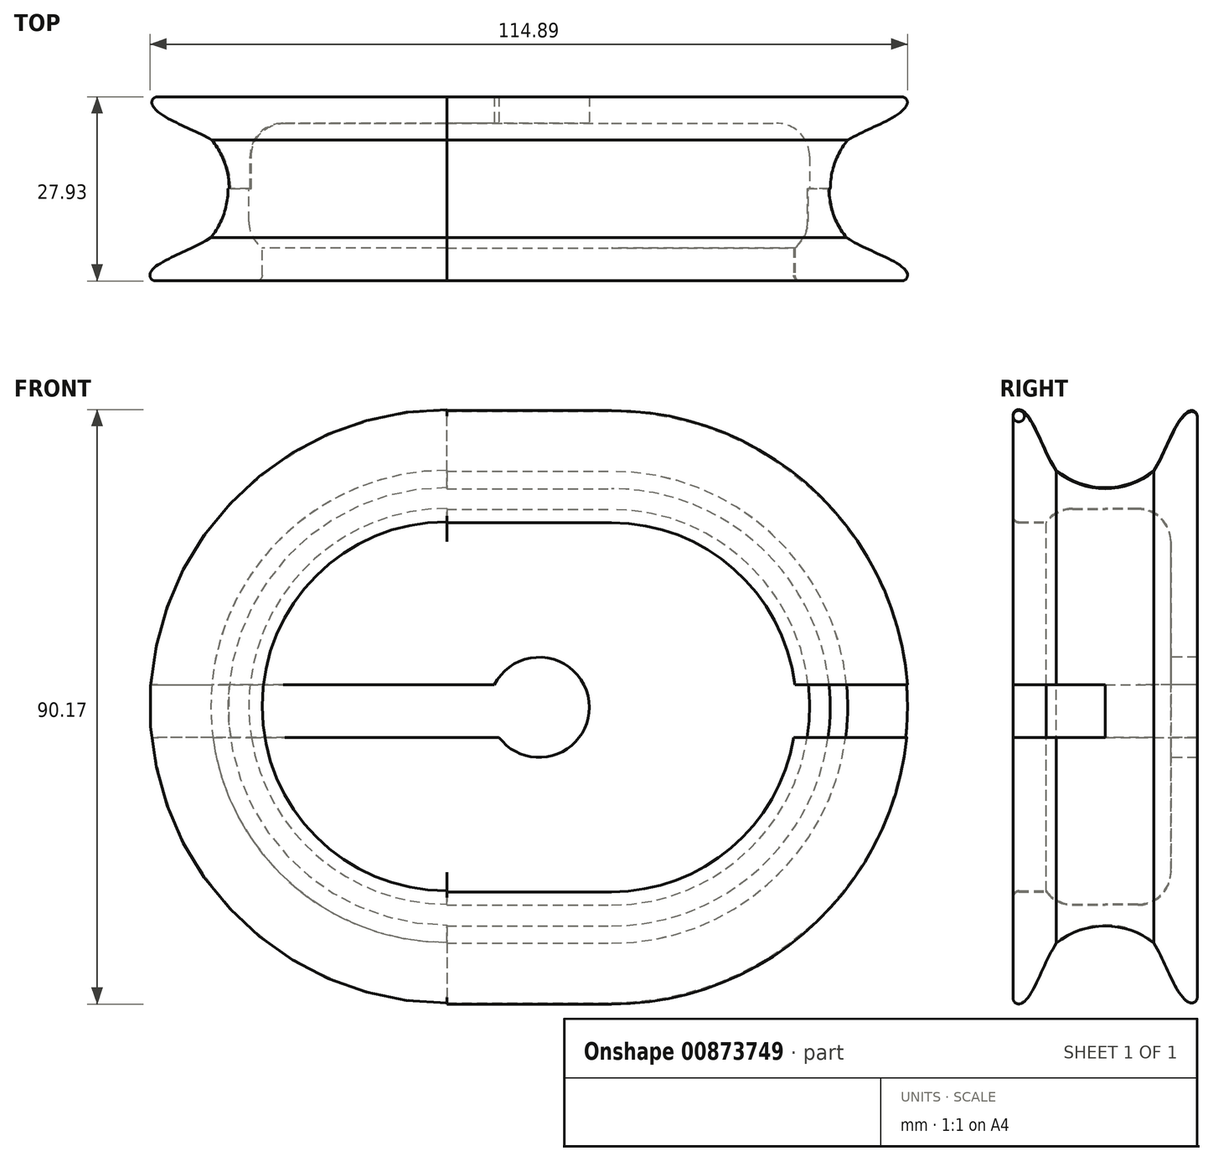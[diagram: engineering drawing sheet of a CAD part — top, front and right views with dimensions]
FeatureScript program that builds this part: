
annotation { "Feature Type Name" : "Feature", "Feature Type Description" : "" }
export const myFeature = defineFeature(function(context is Context, id is Id, definition is map)
    precondition{}
    {
        {
            var Q0;
            Q0=qCreatedBy(makeId("Top.planeOp"),FACE);
            var sketch = newSketch(context, id + "F0", { "sketchPlane" : qUnion([Q0])});
            skLineSegment(sketch, "E0", {"start": v(32.84, -14) * mm, "end": v(32.86, 13.93) * mm, "construction": true});
            skLineSegment(sketch, "E1", {"start": v(44, 13.93) * mm, "end": v(0, 13.93) * mm});
            skLineSegment(sketch, "E2", {"start": v(-31.68, 0) * mm, "end": v(56.18, -0.04) * mm, "construction": true});
            skLineSegment(sketch, "E3", {"start": v(26.86, 4.13) * mm, "end": v(26.83, 4.13) * mm, "construction": true});
            skFitSpline(sketch, "E4", {"points": [v(32.95, 4.2) * mm, v(44.88, 13.93) * mm], "startDerivative": vector(2.93, 13.74) * mm, "endDerivative": vector(-3.03, 11.76) * mm});
            skFitSpline(sketch, "E5.MirrorCS", {"points": [v(33.4, -4.44) * mm, v(44.71, -14) * mm], "startDerivative": vector(1.94, -13.96) * mm, "endDerivative": vector(-7.31, -9.9) * mm});
            skLineSegment(sketch, "E6", {"start": v(30.01, 4.92) * mm, "end": v(30.01, -0.03) * mm});
            skLineSegment(sketch, "E7", {"start": v(0, 9.93) * mm, "end": v(0, 13.93) * mm});
            skArc(sketch, "E8.filletArc", {"start": v(30.01, 4.92) * mm, "mid": v(28.55, 8.46) * mm, "end": v(25.01, 9.92) * mm});
            skArc(sketch, "E9.MirrorCS", {"start": v(30, -4.98) * mm, "mid": v(29.47, -7.22) * mm, "end": v(28, -8.99) * mm});
            skLineSegment(sketch, "E10.MirrorCS", {"start": v(30, -4.98) * mm, "end": v(30.01, -0.03) * mm});
            skLineSegment(sketch, "E11", {"start": v(28, -13.13) * mm, "end": v(28, -8.99) * mm});
            skLineSegment(sketch, "E12", {"start": v(4.88, 3.85) * mm, "end": v(44.88, 3.83) * mm, "construction": true});
            skLineSegment(sketch, "E13", {"start": v(44.88, 18.61) * mm, "end": v(44.88, -32.14) * mm, "construction": true});
            skLineSegment(sketch, "E14", {"start": v(25.01, 9.92) * mm, "end": v(0, 9.93) * mm});
            skLineSegment(sketch, "E15", {"start": v(44.15, -14) * mm, "end": v(28.85, -13.99) * mm});
            skLineSegment(sketch, "E16", {"start": v(36.5, -1.52) * mm, "end": v(36.51, 2.9) * mm, "construction": true});
            skArc(sketch, "E17", {"start": v(35.8, 7.37) * mm, "mid": v(33.16, -0.03) * mm, "end": v(35.8, -7.44) * mm});
            skArc(sketch, "E18.filletArc", {"start": v(44.15, -14) * mm, "mid": v(44.82, -13.68) * mm, "end": v(44.99, -12.96) * mm});
            skArc(sketch, "E19.filletArc", {"start": v(44.77, 12.71) * mm, "mid": v(44.72, 13.53) * mm, "end": v(44, 13.93) * mm});
            skPoint(sketch, "E20.visualSharp", {"position": v(28, -13.99) * mm});
            skArc(sketch, "E20.filletArc", {"start": v(28, -13.13) * mm, "mid": v(28.24, -13.74) * mm, "end": v(28.85, -13.99) * mm});
            skLineSegment(sketch, "E21", {"start": v(44, 13.93) * mm, "end": v(44.17, -17.26) * mm, "construction": true});
            skLineSegment(sketch, "E22", {"start": v(44.15, -14) * mm, "end": v(51.34, -14) * mm, "construction": true});
            skPoint(sketch, "E23", {"position": v(44.15, -14) * mm});
            skSolve(sketch);
        }
        {
            var Q0;
            Q0=qSketchRegion(id+"F0",true);
            var Q1;
            Q1=qSketchRegion(id+"F0",true);
            var Q2;
            Q2=makeQuery(id+"F0.imprint","IMPRINT",FACE,{"disambiguationData":[TD([[makeQuery(id+"F0.imprint","IMPRINT",EDGE,{"derivedFrom":sQuery(id+"F0.wireOp",EDGE,"E1")}),1.0]])]});
            var Q3;
            Q3=sQuery(id+"F0.wireOp",EDGE,"YOEqnzkB-9UwB-SSfj-woJi-8cwrd5BflBc7");
            var Q4;
            Q4=sQuery(id+"F0.wireOp",EDGE,"E7");
            revolve(context, id + "F1", {"surfaceOperationType" : NewSurfaceOperationType.NEW, "entities" : qUnion([Q0, Q1, Q2]), "axis" : qUnion([Q3, Q4]), "revolveType" : RevolveType.SYMMETRIC, "angle" : 180 * degree});
        }
        {
            var Q0;
            Q0=makeQuery(id+"F1.opRevolve","CAP_FACE",FACE,{"disambiguationData":[OSD([sQuery(id+"F0.wireOp",EDGE,"E1"),sQuery(id+"F0.wireOp",EDGE,"E4"),sQuery(id+"F0.wireOp",EDGE,"pFRlobtz-0q4r-BGyK-Zf5O-oVfqoQiTMujq"),sQuery(id+"F0.wireOp",EDGE,"0d47ac5b-4a7f-461a-a2c7-a7ca7c96fb220.MirrorCS"),sQuery(id+"F0.wireOp",EDGE,"E5.MirrorCS"),sQuery(id+"F0.wireOp",EDGE,"mUEO9S0t-vfNT-DUiq-7ehG-LlwwYBXUM1qr"),sQuery(id+"F0.wireOp",EDGE,"E6"),sQuery(id+"F0.wireOp",EDGE,"E7"),sQuery(id+"F0.wireOp",EDGE,"E8.filletArc"),sQuery(id+"F0.wireOp",EDGE,"E9.MirrorCS"),sQuery(id+"F0.wireOp",EDGE,"E10.MirrorCS"),sQuery(id+"F0.wireOp",EDGE,"DfFPZrzA-9eie-ccyR-lrFW-XJ07qiCjYuLb"),sQuery(id+"F0.wireOp",EDGE,"E11")])],"isStart":false});
            extrude(context, id + "F2", {"entities" : qUnion([Q0]), "operationType" : NewBodyOperationType.ADD, "depth" : 25 * mm, "offsetDistance" : 25 * mm});
        }
        {
            var Q0;
            Q0=makeQuery(id+"F2.opExtrude","CAP_FACE",FACE,{"disambiguationData":[OSD([sQuery(id+"F0.wireOp",EDGE,"E1"),sQuery(id+"F0.wireOp",EDGE,"E4"),sQuery(id+"F0.wireOp",EDGE,"pFRlobtz-0q4r-BGyK-Zf5O-oVfqoQiTMujq"),sQuery(id+"F0.wireOp",EDGE,"0d47ac5b-4a7f-461a-a2c7-a7ca7c96fb220.MirrorCS"),sQuery(id+"F0.wireOp",EDGE,"E5.MirrorCS"),sQuery(id+"F0.wireOp",EDGE,"mUEO9S0t-vfNT-DUiq-7ehG-LlwwYBXUM1qr"),sQuery(id+"F0.wireOp",EDGE,"E6"),sQuery(id+"F0.wireOp",EDGE,"E7"),sQuery(id+"F0.wireOp",EDGE,"E8.filletArc"),sQuery(id+"F0.wireOp",EDGE,"E9.MirrorCS"),sQuery(id+"F0.wireOp",EDGE,"E10.MirrorCS"),sQuery(id+"F0.wireOp",EDGE,"DfFPZrzA-9eie-ccyR-lrFW-XJ07qiCjYuLb"),sQuery(id+"F0.wireOp",EDGE,"E11")])],"isStart":false});
            cPlane(context, id + "F3", {"entities" : qUnion([Q0]), "cplaneType" : CPlaneType.OFFSET, "offset" : 0 * mm, "width" : 150 * mm, "height" : 150 * mm});
        }
        {
            var Q0;
            Q0=qCreatedBy(id+"F3.planeOp",FACE);
            var sketch = newSketch(context, id + "F4", { "sketchPlane" : qUnion([Q0])});
            skLineSegment(sketch, "E24", {"start": v(-153.79, 55.07) * mm, "end": v(-241.65, 55.1) * mm, "construction": true});
            skLineSegment(sketch, "E25", {"start": v(-185.46, 96.49) * mm, "end": v(-185.5, 8.68) * mm, "construction": true});
            skLineSegment(sketch, "E26", {"start": v(-174.35, 54.1) * mm, "end": v(-202.27, 54.12) * mm, "construction": true});
            skLineSegment(sketch, "E27", {"start": v(-202.27, 65.26) * mm, "end": v(-202.27, 21.26) * mm});
            skLineSegment(sketch, "E28", {"start": v(-188.34, -10.41) * mm, "end": v(-188.3, 77.45) * mm, "construction": true});
            skLineSegment(sketch, "E29", {"start": v(-192.47, 48.13) * mm, "end": v(-192.47, 48.1) * mm, "construction": true});
            skFitSpline(sketch, "E30", {"points": [v(-192.54, 54.22) * mm, v(-202.27, 66.15) * mm], "startDerivative": vector(-13.74, 2.93) * mm, "endDerivative": vector(-11.76, -3.03) * mm});
            skFitSpline(sketch, "E31.MirrorCS", {"points": [v(-183.9, 54.67) * mm, v(-174.35, 65.98) * mm], "startDerivative": vector(13.96, 1.94) * mm, "endDerivative": vector(9.9, -7.31) * mm});
            skLineSegment(sketch, "E32", {"start": v(-193.27, 51.28) * mm, "end": v(-188.31, 51.28) * mm});
            skLineSegment(sketch, "E33", {"start": v(-198.27, 21.26) * mm, "end": v(-202.27, 21.26) * mm});
            skArc(sketch, "E34.filletArc", {"start": v(-193.27, 51.28) * mm, "mid": v(-196.8, 49.81) * mm, "end": v(-198.27, 46.28) * mm});
            skArc(sketch, "E35.MirrorCS", {"start": v(-183.36, 51.27) * mm, "mid": v(-181.12, 50.74) * mm, "end": v(-179.36, 49.26) * mm});
            skLineSegment(sketch, "E36.MirrorCS", {"start": v(-183.36, 51.27) * mm, "end": v(-188.31, 51.28) * mm});
            skLineSegment(sketch, "E37", {"start": v(-175.21, 49.26) * mm, "end": v(-179.36, 49.26) * mm});
            skLineSegment(sketch, "E38", {"start": v(-192.2, 26.15) * mm, "end": v(-192.18, 66.15) * mm, "construction": true});
            skLineSegment(sketch, "E39", {"start": v(-206.96, 66.15) * mm, "end": v(-156.2, 66.15) * mm, "construction": true});
            skLineSegment(sketch, "E40", {"start": v(-198.27, 46.28) * mm, "end": v(-198.27, 21.26) * mm});
            skLineSegment(sketch, "E41", {"start": v(-174.35, 65.42) * mm, "end": v(-174.36, 50.11) * mm});
            skLineSegment(sketch, "E42", {"start": v(-186.82, 57.77) * mm, "end": v(-191.24, 57.78) * mm, "construction": true});
            skArc(sketch, "E43", {"start": v(-195.71, 57.06) * mm, "mid": v(-188.31, 54.42) * mm, "end": v(-180.9, 57.06) * mm});
            skArc(sketch, "E44.filletArc", {"start": v(-174.35, 65.42) * mm, "mid": v(-174.67, 66.08) * mm, "end": v(-175.38, 66.25) * mm});
            skArc(sketch, "E45.filletArc", {"start": v(-201.06, 66.04) * mm, "mid": v(-201.88, 65.98) * mm, "end": v(-202.27, 65.26) * mm});
            skPoint(sketch, "E46.visualSharp", {"position": v(-174.36, 49.26) * mm});
            skArc(sketch, "E46.filletArc", {"start": v(-175.21, 49.26) * mm, "mid": v(-174.6, 49.5) * mm, "end": v(-174.36, 50.11) * mm});
            skLineSegment(sketch, "E47", {"start": v(-202.27, 65.26) * mm, "end": v(-171.09, 65.44) * mm, "construction": true});
            skLineSegment(sketch, "E48", {"start": v(-174.35, 65.42) * mm, "end": v(-174.35, 72.6) * mm, "construction": true});
            skPoint(sketch, "E49", {"position": v(-174.35, 65.42) * mm});
            skLineSegment(sketch, "E50", {"start": v(34.56, 33.95) * mm, "end": v(-53.3, 34) * mm, "construction": true});
            skLineSegment(sketch, "E51", {"start": v(2.88, 75.37) * mm, "end": v(2.84, -12.43) * mm, "construction": true});
            skLineSegment(sketch, "E52", {"start": v(14, 33) * mm, "end": v(-13.93, 33) * mm, "construction": true});
            skLineSegment(sketch, "E53", {"start": v(-13.93, 44.15) * mm, "end": v(-13.93, 0.15) * mm});
            skLineSegment(sketch, "E54", {"start": v(0, -31.53) * mm, "end": v(0.04, 56.33) * mm, "construction": true});
            skLineSegment(sketch, "E55", {"start": v(-4.13, 27.01) * mm, "end": v(-4.13, 26.98) * mm, "construction": true});
            skFitSpline(sketch, "E56", {"points": [v(-4.2, 33.1) * mm, v(-13.93, 45.04) * mm], "startDerivative": vector(-13.74, 2.93) * mm, "endDerivative": vector(-11.76, -3.03) * mm});
            skFitSpline(sketch, "E57.MirrorCS", {"points": [v(4.44, 33.55) * mm, v(14, 44.86) * mm], "startDerivative": vector(13.96, 1.94) * mm, "endDerivative": vector(9.9, -7.31) * mm});
            skLineSegment(sketch, "E58", {"start": v(-4.92, 30.16) * mm, "end": v(0.03, 30.16) * mm});
            skLineSegment(sketch, "E59", {"start": v(-9.93, 0.15) * mm, "end": v(-13.93, 0.15) * mm});
            skArc(sketch, "E60.filletArc", {"start": v(-4.92, 30.16) * mm, "mid": v(-8.46, 28.7) * mm, "end": v(-9.92, 25.16) * mm});
            skArc(sketch, "E61.MirrorCS", {"start": v(4.98, 30.16) * mm, "mid": v(7.22, 29.62) * mm, "end": v(8.99, 28.14) * mm});
            skLineSegment(sketch, "E62.MirrorCS", {"start": v(4.98, 30.16) * mm, "end": v(0.03, 30.16) * mm});
            skLineSegment(sketch, "E63", {"start": v(13.13, 28.14) * mm, "end": v(8.99, 28.14) * mm});
            skLineSegment(sketch, "E64", {"start": v(-3.85, 5.04) * mm, "end": v(-3.83, 45.04) * mm, "construction": true});
            skLineSegment(sketch, "E65", {"start": v(-18.61, 45.04) * mm, "end": v(32.14, 45.04) * mm, "construction": true});
            skLineSegment(sketch, "E66", {"start": v(-9.92, 25.16) * mm, "end": v(-9.93, 0.15) * mm});
            skLineSegment(sketch, "E67", {"start": v(14, 44.3) * mm, "end": v(13.99, 29) * mm});
            skLineSegment(sketch, "E68", {"start": v(1.52, 36.66) * mm, "end": v(-2.9, 36.66) * mm, "construction": true});
            skArc(sketch, "E69", {"start": v(-7.37, 35.94) * mm, "mid": v(0.03, 33.3) * mm, "end": v(7.44, 35.94) * mm});
            skArc(sketch, "E70.filletArc", {"start": v(14, 44.3) * mm, "mid": v(13.68, 44.97) * mm, "end": v(12.96, 45.14) * mm});
            skArc(sketch, "E71.filletArc", {"start": v(-12.71, 44.92) * mm, "mid": v(-13.53, 44.87) * mm, "end": v(-13.93, 44.15) * mm});
            skPoint(sketch, "E72.visualSharp", {"position": v(13.99, 28.14) * mm});
            skArc(sketch, "E72.filletArc", {"start": v(13.13, 28.14) * mm, "mid": v(13.74, 28.4) * mm, "end": v(13.99, 29) * mm});
            skLineSegment(sketch, "E73", {"start": v(-13.93, 44.15) * mm, "end": v(17.26, 44.32) * mm, "construction": true});
            skLineSegment(sketch, "E74", {"start": v(14, 44.3) * mm, "end": v(14, 51.5) * mm, "construction": true});
            skPoint(sketch, "E75", {"position": v(14, 44.3) * mm});
            skSolve(sketch);
        }
        {
            var Q0;
            Q0=makeQuery(id+"F4.imprint","IMPRINT",FACE,{"disambiguationData":[TD([[makeQuery(id+"F4.imprint","IMPRINT",EDGE,{"derivedFrom":sQuery(id+"F4.wireOp",EDGE,"E53")}),1.0]])]});
            var Q1;
            Q1=sQuery(id+"F4.wireOp",EDGE,"E59");
            revolve(context, id + "F5", {"operationType" : NewBodyOperationType.ADD, "surfaceOperationType" : NewSurfaceOperationType.NEW, "entities" : qUnion([Q0]), "axis" : qUnion([Q1]), "revolveType" : RevolveType.ONE_DIRECTION, "oppositeDirection" : true, "angle" : 180 * degree});
        }
        {
            var Q0;
            Q0=qCreatedBy(makeId("Front.planeOp"),FACE);
            var sketch = newSketch(context, id + "F6", { "sketchPlane" : qUnion([Q0])});
            skLineSegment(sketch, "E76", {"start": v(29.26, 0) * mm, "end": v(-58.04, 0) * mm, "construction": true});
            skLineSegment(sketch, "E77", {"start": v(-10.99, -28.68) * mm, "end": v(-10.99, 40.74) * mm, "construction": true});
            skLineSegment(sketch, "E78.bottom", {"start": v(-17.8, 3.43) * mm, "end": v(-45.99, 3.43) * mm});
            skLineSegment(sketch, "E78.top", {"start": v(-17.09, -4.57) * mm, "end": v(-45.99, -4.57) * mm});
            skPoint(sketch, "E79", {"position": v(-10.99, 0) * mm});
            skArc(sketch, "E80", {"start": v(-17.8, 3.43) * mm, "mid": v(-3.4, 0.67) * mm, "end": v(-17.09, -4.57) * mm});
            skLineSegment(sketch, "E81", {"start": v(-71.37, 3.43) * mm, "end": v(-71.37, -4.57) * mm});
            skLineSegment(sketch, "E82", {"start": v(-71.37, -4.57) * mm, "end": v(-45.99, -4.57) * mm});
            skLineSegment(sketch, "E83", {"start": v(-45.99, 3.43) * mm, "end": v(-71.37, 3.43) * mm});
            skLineSegment(sketch, "E84", {"start": v(-9.35, 3.43) * mm, "end": v(-9.35, -4.57) * mm, "construction": true});
            skLineSegment(sketch, "E85", {"start": v(47.39, 3.43) * mm, "end": v(-4.18, 3.43) * mm});
            skLineSegment(sketch, "E86", {"start": v(-4.89, -4.57) * mm, "end": v(47.39, -4.57) * mm});
            skLineSegment(sketch, "E87", {"start": v(47.39, 3.43) * mm, "end": v(47.39, -4.57) * mm});
            skSolve(sketch);
        }
        {
            var Q0;
            Q0=makeQuery(id+"F6.imprint","IMPRINT",FACE,{"disambiguationData":[TD([[makeQuery(id+"F6.imprint","IMPRINT",EDGE,{"derivedFrom":sQuery(id+"F6.wireOp",EDGE,"E78.bottom")}),1.0]])]});
            extrude(context, id + "F7", {"entities" : qUnion([Q0]), "operationType" : NewBodyOperationType.REMOVE, "oppositeDirection" : true, "depth" : 15 * mm, "offsetDistance" : 25 * mm});
        }
        {
            var Q0;
            {var subQ0=sQuery(id+"F6.wireOp",EDGE,"E85");Q0=makeQuery(id+"F6.imprint","IMPRINT",FACE,{"disambiguationData":[TD([[makeQuery(id+"F6.imprint","IMPRINT",EDGE,{"derivedFrom":subQ0}),1.0]])]});}
            extrude(context, id + "F8", {"entities" : qUnion([Q0]), "operationType" : NewBodyOperationType.REMOVE, "depth" : 20 * mm, "offsetDistance" : 25 * mm});
        }
    });
